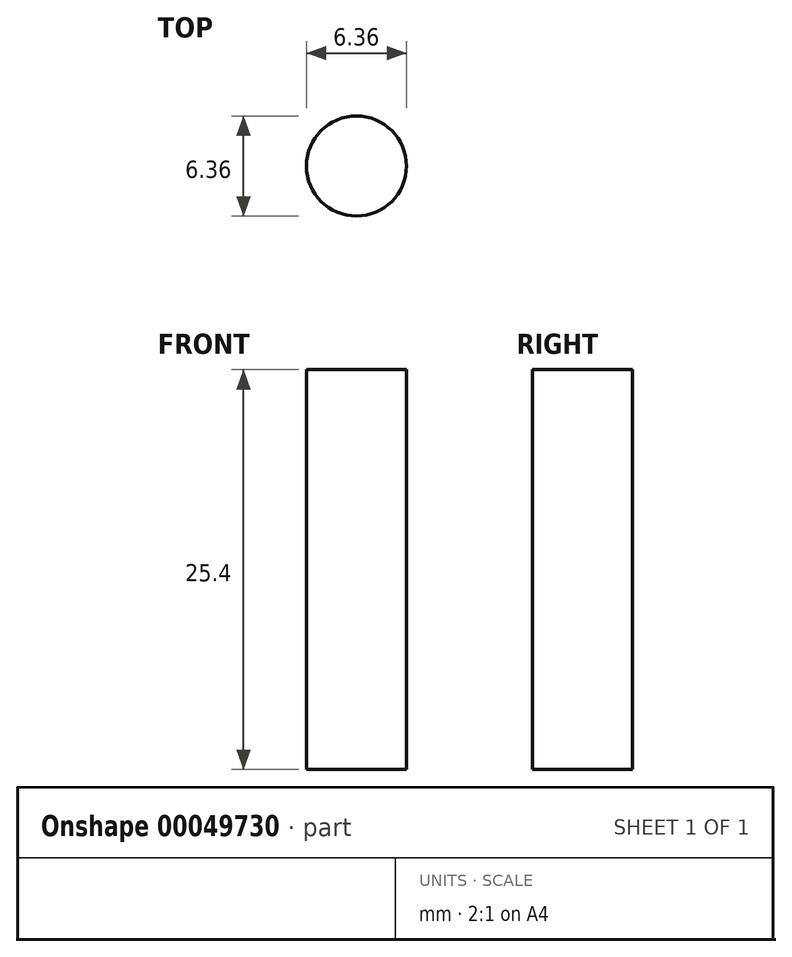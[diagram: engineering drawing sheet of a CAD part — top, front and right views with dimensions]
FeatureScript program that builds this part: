
annotation { "Feature Type Name" : "Feature", "Feature Type Description" : "" }
export const myFeature = defineFeature(function(context is Context, id is Id, definition is map)
    precondition{}
    {
        {
            var Q0;
            Q0=qCreatedBy(makeId("Top.planeOp"),FACE);
            var sketch = newSketch(context, id + "F0", { "sketchPlane" : qUnion([Q0])});
            skCircle(sketch, "E0", {"center": v(0, 0) * mm, "radius": 3.18 * mm});
            skSolve(sketch);
        }
        {
            var Q0;
            Q0 = qSketchRegion(id + "F0", true);
            extrude(context, id + "F1", {"entities" : qUnion([Q0]), "depth" : 25.4 * mm});
        }
    });
